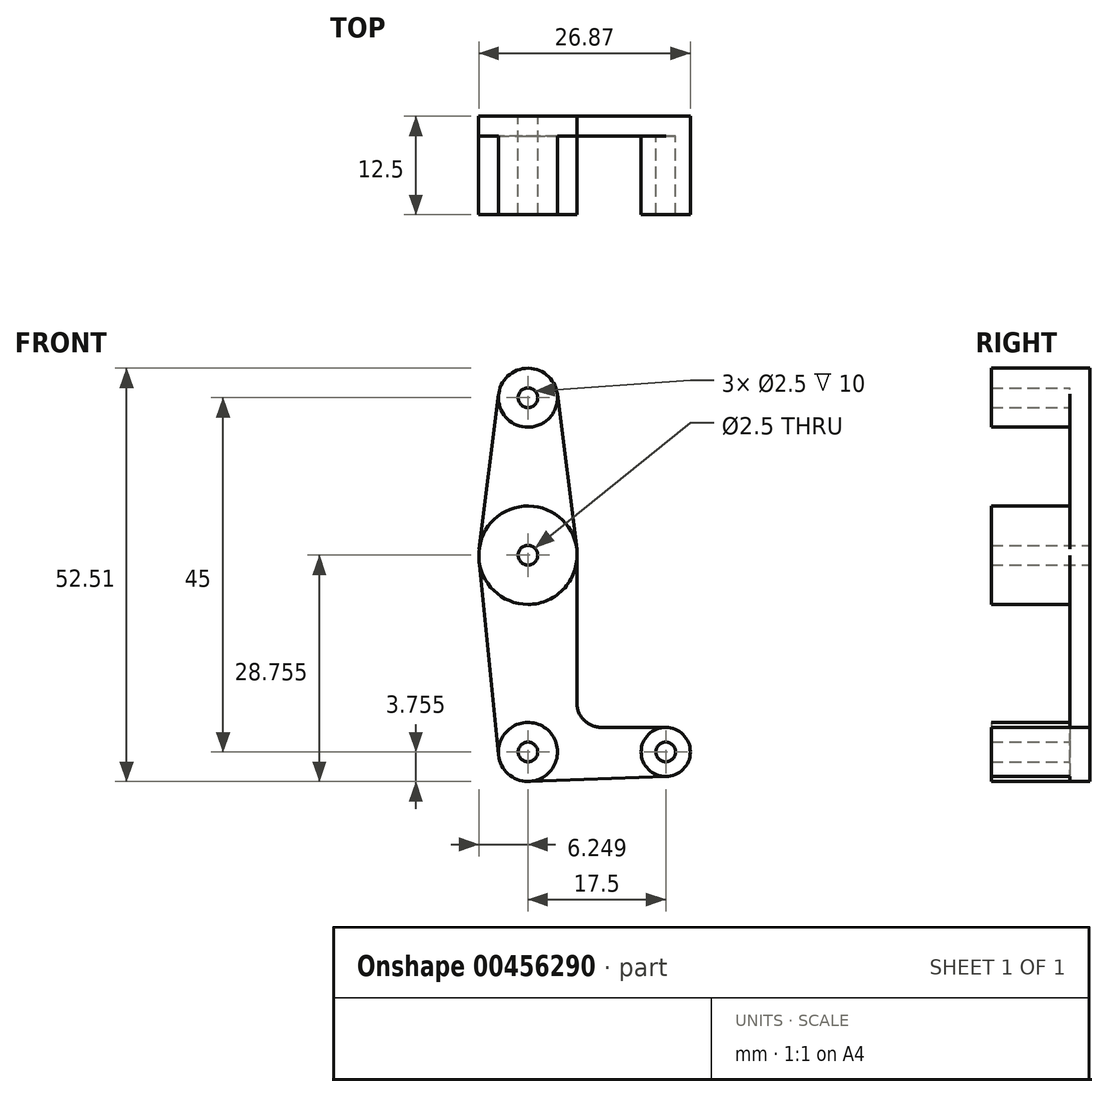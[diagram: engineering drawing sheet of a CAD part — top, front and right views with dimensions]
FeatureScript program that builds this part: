
annotation { "Feature Type Name" : "Feature", "Feature Type Description" : "" }
export const myFeature = defineFeature(function(context is Context, id is Id, definition is map)
    precondition{}
    {
        {
            var Q0;
            Q0=qCreatedBy(makeId("Front.planeOp"),FACE);
            var sketch = newSketch(context, id + "F0", { "sketchPlane" : qUnion([Q0])});
            skCircle(sketch, "E0", {"center": v(-6.2, 41.87) * mm, "radius": 3.75 * mm});
            skCircle(sketch, "E1", {"center": v(-6.2, 21.87) * mm, "radius": 6.25 * mm});
            skCircle(sketch, "E2", {"center": v(-6.2, -3.13) * mm, "radius": 3.75 * mm});
            skCircle(sketch, "E3", {"center": v(11.3, -3.12) * mm, "radius": 3.12 * mm});
            skLineSegment(sketch, "E4", {"start": v(0, 3.13) * mm, "end": v(0.05, 21.86) * mm});
            skLineSegment(sketch, "E5", {"start": v(0, 22.66) * mm, "end": v(-2.48, 42.34) * mm});
            skLineSegment(sketch, "E6", {"start": v(-9.92, 42.34) * mm, "end": v(-12.4, 22.66) * mm});
            skLineSegment(sketch, "E7", {"start": v(-6.2, 41.87) * mm, "end": v(-6.2, 21.87) * mm});
            skLineSegment(sketch, "E8", {"start": v(-6.2, -3.13) * mm, "end": v(11.3, -3.13) * mm});
            skLineSegment(sketch, "E9", {"start": v(-6.2, 21.87) * mm, "end": v(-6.2, -3.13) * mm});
            skLineSegment(sketch, "E10", {"start": v(3.13, 0) * mm, "end": v(11.3, 0) * mm});
            skCircle(sketch, "E11", {"center": v(-6.2, 41.87) * mm, "radius": 1.25 * mm});
            skCircle(sketch, "E12", {"center": v(-6.2, 21.87) * mm, "radius": 1.25 * mm});
            skCircle(sketch, "E13", {"center": v(-6.2, -3.13) * mm, "radius": 1.25 * mm});
            skCircle(sketch, "E14", {"center": v(11.3, -3.12) * mm, "radius": 1.25 * mm});
            skPoint(sketch, "E15.visualSharp", {"position": v(0, 0) * mm});
            skLineSegment(sketch, "E16", {"start": v(-6.07, -6.87) * mm, "end": v(11.41, -6.25) * mm});
            skLineSegment(sketch, "E17", {"start": v(-12.42, 21.25) * mm, "end": v(-9.93, -3.5) * mm});
            skArc(sketch, "E18.filletArc", {"start": v(0, 3.13) * mm, "mid": v(0.92, 0.92) * mm, "end": v(3.13, 0) * mm});
            skSolve(sketch);
        }
        {
            var Q0;
            Q0 = qSketchRegion(id + "F0", true);
            var Q1;
            {var subQ0=sQuery(id+"F0.wireOp",EDGE,"E9");var subQ1=sQuery(id+"F0.wireOp",EDGE,"E2");var subQ2=makeQuery(id+"F0.imprint","INTERSECT",VERTEX,{"derivedFrom":[subQ1,subQ0]});Q1=makeQuery(id+"F0.imprint","IMPRINT",FACE,{"disambiguationData":[TD([[makeQuery(id+"F0.imprint","IMPRINT",EDGE,{"disambiguationData":[TD([[subQ2,1.0]])],"derivedFrom":subQ1}),1.0]])]});}
            var Q2;
            {var subQ0=sQuery(id+"F0.wireOp",EDGE,"E9");var subQ1=sQuery(id+"F0.wireOp",EDGE,"E8");var subQ2=makeQuery(id+"F0.imprint","INTERSECT",VERTEX,{"derivedFrom":[subQ1,subQ0]});Q2=makeQuery(id+"F0.imprint","IMPRINT",FACE,{"disambiguationData":[TD([[makeQuery(id+"F0.imprint","IMPRINT",EDGE,{"disambiguationData":[TD([[subQ2,-1.0]])],"derivedFrom":subQ1}),-1.0]])]});}
            var Q3;
            {var subQ0=sQuery(id+"F0.wireOp",EDGE,"E9");var subQ1=sQuery(id+"F0.wireOp",EDGE,"E8");var subQ2=makeQuery(id+"F0.imprint","INTERSECT",VERTEX,{"derivedFrom":[subQ1,subQ0]});Q3=makeQuery(id+"F0.imprint","IMPRINT",FACE,{"disambiguationData":[TD([[makeQuery(id+"F0.imprint","IMPRINT",EDGE,{"disambiguationData":[TD([[subQ2,-1.0]])],"derivedFrom":subQ1}),1.0]])]});}
            var Q4;
            Q4=makeQuery(id+"F0.imprint","IMPRINT",FACE,{"disambiguationData":[TD([[makeQuery(id+"F0.imprint","IMPRINT",EDGE,{"derivedFrom":sQuery(id+"F0.wireOp",EDGE,"E14")}),1.0]])]});
            var Q5;
            Q5=makeQuery(id+"F0.imprint","IMPRINT",FACE,{"disambiguationData":[TD([[makeQuery(id+"F0.imprint","IMPRINT",EDGE,{"derivedFrom":sQuery(id+"F0.wireOp",EDGE,"E11")}),1.0]])]});
            extrude(context, id + "F1", {"entities" : qUnion([Q0, Q1, Q2, Q3, Q4, Q5]), "depth" : 2.5 * mm, "offsetDistance" : 25 * mm});
        }
        {
            var Q0;
            {var subQ0=sQuery(id+"F0.wireOp",EDGE,"E1");var subQ8=makeQuery(id+"F0.imprint","INTERSECT",VERTEX,{"derivedFrom":[subQ0,sQuery(id+"F0.wireOp",EDGE,"E6")]});Q0=makeQuery(id+"F0.imprint","IMPRINT",FACE,{"disambiguationData":[TD([[makeQuery(id+"F0.imprint","IMPRINT",EDGE,{"disambiguationData":[TD([[subQ8,1.0]])],"derivedFrom":subQ0}),1.0]])]});}
            var Q1;
            {var subQ1=sQuery(id+"F0.wireOp",EDGE,"E1");var subQ8=makeQuery(id+"F0.imprint","INTERSECT",VERTEX,{"derivedFrom":[subQ1,sQuery(id+"F0.wireOp",EDGE,"E5")]});Q1=makeQuery(id+"F0.imprint","IMPRINT",FACE,{"disambiguationData":[TD([[makeQuery(id+"F0.imprint","IMPRINT",EDGE,{"disambiguationData":[TD([[subQ8,-1.0]])],"derivedFrom":subQ1}),1.0]])]});}
            var Q2;
            Q2=makeQuery(id+"F0.imprint","IMPRINT",FACE,{"disambiguationData":[TD([[makeQuery(id+"F0.imprint","IMPRINT",EDGE,{"derivedFrom":sQuery(id+"F0.wireOp",EDGE,"E11")}),-1.0]])]});
            var Q3;
            Q3=makeQuery(id+"F0.imprint","IMPRINT",FACE,{"disambiguationData":[TD([[makeQuery(id+"F0.imprint","IMPRINT",EDGE,{"derivedFrom":sQuery(id+"F0.wireOp",EDGE,"E14")}),-1.0]])]});
            var Q4;
            {var subQ0=sQuery(id+"F0.wireOp",EDGE,"E9");var subQ1=sQuery(id+"F0.wireOp",EDGE,"E2");var subQ2=makeQuery(id+"F0.imprint","INTERSECT",VERTEX,{"derivedFrom":[subQ1,subQ0]});Q4=makeQuery(id+"F0.imprint","IMPRINT",FACE,{"disambiguationData":[TD([[makeQuery(id+"F0.imprint","IMPRINT",EDGE,{"disambiguationData":[TD([[subQ2,1.0]])],"derivedFrom":subQ1}),1.0]])]});}
            var Q5;
            {var subQ1=sQuery(id+"F0.wireOp",EDGE,"E2");var subQ6=makeQuery(id+"F0.imprint","INTERSECT",VERTEX,{"derivedFrom":[subQ1,sQuery(id+"F0.wireOp",EDGE,"E17")]});Q5=makeQuery(id+"F0.imprint","IMPRINT",FACE,{"disambiguationData":[TD([[makeQuery(id+"F0.imprint","IMPRINT",EDGE,{"disambiguationData":[TD([[subQ6,1.0]])],"derivedFrom":subQ1}),1.0]])]});}
            extrude(context, id + "F2", {"entities" : qUnion([Q0, Q1, Q2, Q3, Q4, Q5]), "operationType" : NewBodyOperationType.ADD, "depth" : 12.5 * mm, "offsetDistance" : 25 * mm});
        }
    });
